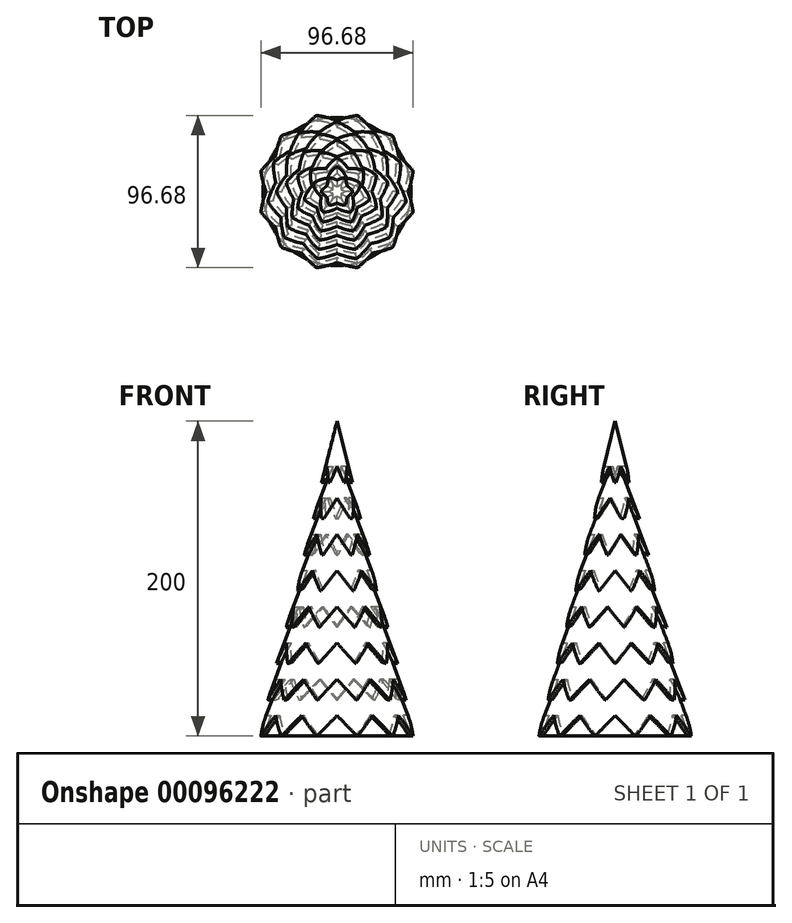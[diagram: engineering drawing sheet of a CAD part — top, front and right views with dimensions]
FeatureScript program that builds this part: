
annotation { "Feature Type Name" : "Feature", "Feature Type Description" : "" }
export const myFeature = defineFeature(function(context is Context, id is Id, definition is map)
    precondition{}
    {
        {
            var Q0;
            Q0=qCreatedBy(makeId("Front.planeOp"),FACE);
            var sketch = newSketch(context, id + "F0", { "sketchPlane" : qUnion([Q0])});
            skLineSegment(sketch, "E0", {"start": v(0, 0) * mm, "end": v(0, 200) * mm});
            skLineSegment(sketch, "E1", {"start": v(-50, 0) * mm, "end": v(0, 0) * mm});
            skLineSegment(sketch, "E2", {"start": v(-50, 0) * mm, "end": v(-41.24, 23.03) * mm});
            skLineSegment(sketch, "E3", {"start": v(-41.24, 23.03) * mm, "end": v(-44.24, 23.03) * mm});
            skLineSegment(sketch, "E4", {"start": v(-44.24, 23.03) * mm, "end": v(-35.49, 46.06) * mm});
            skLineSegment(sketch, "E5", {"start": v(-35.49, 46.06) * mm, "end": v(-38.49, 46.06) * mm});
            skLineSegment(sketch, "E6", {"start": v(-38.49, 46.06) * mm, "end": v(-29.73, 69.08) * mm});
            skLineSegment(sketch, "E7", {"start": v(-29.73, 69.08) * mm, "end": v(-32.73, 69.08) * mm});
            skLineSegment(sketch, "E8", {"start": v(-32.73, 69.08) * mm, "end": v(-23.97, 92.11) * mm});
            skLineSegment(sketch, "E9", {"start": v(-23.97, 92.11) * mm, "end": v(-26.97, 92.11) * mm});
            skLineSegment(sketch, "E10", {"start": v(-26.97, 92.11) * mm, "end": v(-18.22, 115.14) * mm});
            skLineSegment(sketch, "E11", {"start": v(-18.22, 115.14) * mm, "end": v(-21.22, 115.14) * mm});
            skLineSegment(sketch, "E12", {"start": v(-21.22, 115.14) * mm, "end": v(-12.46, 138.17) * mm});
            skLineSegment(sketch, "E13", {"start": v(-12.46, 138.17) * mm, "end": v(-15.46, 138.17) * mm});
            skLineSegment(sketch, "E14", {"start": v(-15.46, 138.17) * mm, "end": v(-6.7, 161.2) * mm});
            skLineSegment(sketch, "E15", {"start": v(-6.7, 161.2) * mm, "end": v(-9.7, 161.2) * mm});
            skLineSegment(sketch, "E16", {"start": v(-9.7, 161.2) * mm, "end": v(0, 200) * mm});
            skLineSegment(sketch, "E17", {"start": v(-50, 0) * mm, "end": v(0, 200) * mm, "construction": true});
            skLineSegment(sketch, "E18.0", {"start": v(-53.2, 0) * mm, "end": v(-48.27, 13) * mm});
            skLineSegment(sketch, "E19", {"start": v(-53.2, 0) * mm, "end": v(-50, 0) * mm});
            skLineSegment(sketch, "E20", {"start": v(-48.27, 13) * mm, "end": v(-45.06, 13) * mm});
            skSolve(sketch);
        }
        {
            var Q0;
            Q0=makeQuery(id+"F0.imprint","IMPRINT",FACE,{"disambiguationData":[TD([[makeQuery(id+"F0.imprint","IMPRINT",EDGE,{"derivedFrom":sQuery(id+"F0.wireOp",EDGE,"E0")}),1.0]])]});
            var Q1;
            Q1=sQuery(id+"F0.wireOp",EDGE,"E0");
            revolve(context, id + "F1", {"entities" : qUnion([Q0]), "axis" : qUnion([Q1]), "revolveType" : RevolveType.FULL});
        }
        {
            var Q0;
            Q0=qCreatedBy(makeId("Front.planeOp"),FACE);
            var sketch = newSketch(context, id + "F2", { "sketchPlane" : qUnion([Q0])});
            skLineSegment(sketch, "E21", {"start": v(-12.78, 0) * mm, "end": v(12.78, 0) * mm});
            skLineSegment(sketch, "E22", {"start": v(12.78, 0) * mm, "end": v(0, 13) * mm});
            skLineSegment(sketch, "E23", {"start": v(0, 13) * mm, "end": v(-12.78, 0) * mm});
            skLineSegment(sketch, "E24.direction1", {"start": v(-12.78, 0) * mm, "end": v(12.78, 0) * mm, "construction": true});
            skLineSegment(sketch, "E24.direction2", {"start": v(-12.78, 0) * mm, "end": v(-12.78, 23.03) * mm, "construction": true});
            skLineSegment(sketch, "E25", {"start": v(-8.28, 138.17) * mm, "end": v(8.28, 138.17) * mm});
            skLineSegment(sketch, "E26", {"start": v(8.28, 138.17) * mm, "end": v(0, 151.17) * mm});
            skLineSegment(sketch, "E27", {"start": v(0, 151.17) * mm, "end": v(-8.28, 138.17) * mm});
            skLineSegment(sketch, "E28", {"start": v(-4.35, 161.2) * mm, "end": v(4.35, 161.2) * mm});
            skLineSegment(sketch, "E29", {"start": v(4.35, 161.2) * mm, "end": v(0, 171.2) * mm});
            skLineSegment(sketch, "E30", {"start": v(0, 171.2) * mm, "end": v(-4.35, 161.2) * mm});
            skLineSegment(sketch, "E31", {"start": v(-12.12, 23.03) * mm, "end": v(12.12, 23.03) * mm});
            skLineSegment(sketch, "E32", {"start": v(12.12, 23.03) * mm, "end": v(0, 36.03) * mm});
            skLineSegment(sketch, "E33", {"start": v(0, 36.03) * mm, "end": v(-12.12, 23.03) * mm});
            skLineSegment(sketch, "E34", {"start": v(-11.7, 46.06) * mm, "end": v(11.7, 46.06) * mm});
            skLineSegment(sketch, "E35", {"start": v(11.7, 46.06) * mm, "end": v(0, 59.06) * mm});
            skLineSegment(sketch, "E36", {"start": v(0, 59.06) * mm, "end": v(-11.7, 46.06) * mm});
            skLineSegment(sketch, "E37", {"start": v(-11.1, 69.08) * mm, "end": v(11.1, 69.08) * mm});
            skLineSegment(sketch, "E38", {"start": v(11.1, 69.08) * mm, "end": v(0, 82.08) * mm});
            skLineSegment(sketch, "E39", {"start": v(0, 82.08) * mm, "end": v(-11.1, 69.08) * mm});
            skLineSegment(sketch, "E40", {"start": v(-10.16, 92.11) * mm, "end": v(10.16, 92.11) * mm});
            skLineSegment(sketch, "E41", {"start": v(10.16, 92.11) * mm, "end": v(0, 105.11) * mm});
            skLineSegment(sketch, "E42", {"start": v(0, 105.11) * mm, "end": v(-10.16, 92.11) * mm});
            skLineSegment(sketch, "E43", {"start": v(-8.77, 115.14) * mm, "end": v(8.77, 115.14) * mm});
            skLineSegment(sketch, "E44", {"start": v(-8.77, 115.14) * mm, "end": v(0, 128.14) * mm});
            skLineSegment(sketch, "E45", {"start": v(0, 128.14) * mm, "end": v(8.77, 115.14) * mm});
            skSolve(sketch);
        }
        {
            var Q0;
            Q0=makeQuery(id+"F2.imprint","IMPRINT",FACE,{"disambiguationData":[TD([[makeQuery(id+"F2.imprint","IMPRINT",EDGE,{"derivedFrom":sQuery(id+"F2.wireOp",EDGE,"E21")}),1.0]])]});
            var Q1;
            Q1=makeQuery(id+"F1.opRevolve","SWEPT_FACE",FACE,{"disambiguationData":[OSD([sQuery(id+"F0.wireOp",EDGE,"E4")])]});
            var Q2;
            Q2=makeQuery(id+"F1.opRevolve","SWEPT_FACE",FACE,{"disambiguationData":[OSD([sQuery(id+"F0.wireOp",EDGE,"E2")])]});
            extrude(context, id + "F3", {"entities" : qUnion([Q0]), "endBound" : BoundingType.UP_TO_SURFACE, "endBoundEntityFace" : qUnion([Q1]), "depth" : 25 * mm, "hasSecondDirection" : true, "secondDirectionBound" : SecondDirectionBoundingType.UP_TO_SURFACE, "secondDirectionOppositeDirection" : false, "secondDirectionBoundEntityFace" : qUnion([Q2]), "secondDirectionDepth" : 25 * mm});
        }
        {
            var Q0;
            Q0=makeQuery(id+"F2.imprint","IMPRINT",FACE,{"disambiguationData":[TD([[makeQuery(id+"F2.imprint","IMPRINT",EDGE,{"derivedFrom":sQuery(id+"F2.wireOp",EDGE,"E31")}),1.0]])]});
            var Q1;
            Q1=makeQuery(id+"F1.opRevolve","SWEPT_FACE",FACE,{"disambiguationData":[OSD([sQuery(id+"F0.wireOp",EDGE,"E4")])]});
            var Q2;
            Q2=makeQuery(id+"F1.opRevolve","SWEPT_FACE",FACE,{"disambiguationData":[OSD([sQuery(id+"F0.wireOp",EDGE,"E2")])]});
            extrude(context, id + "F4", {"entities" : qUnion([Q0]), "endBound" : BoundingType.UP_TO_SURFACE, "endBoundEntityFace" : qUnion([Q1]), "depth" : 25 * mm, "hasSecondDirection" : true, "secondDirectionBound" : SecondDirectionBoundingType.UP_TO_SURFACE, "secondDirectionOppositeDirection" : false, "secondDirectionBoundEntityFace" : qUnion([Q2]), "secondDirectionDepth" : 25 * mm});
        }
        {
            var Q0;
            Q0=makeQuery(id+"F2.imprint","IMPRINT",FACE,{"disambiguationData":[TD([[makeQuery(id+"F2.imprint","IMPRINT",EDGE,{"derivedFrom":sQuery(id+"F2.wireOp",EDGE,"E34")}),1.0]])]});
            var Q1;
            Q1=makeQuery(id+"F1.opRevolve","SWEPT_FACE",FACE,{"disambiguationData":[OSD([sQuery(id+"F0.wireOp",EDGE,"E6")])]});
            var Q2;
            Q2=makeQuery(id+"F1.opRevolve","SWEPT_FACE",FACE,{"disambiguationData":[OSD([sQuery(id+"F0.wireOp",EDGE,"E4")])]});
            extrude(context, id + "F5", {"entities" : qUnion([Q0]), "endBound" : BoundingType.UP_TO_SURFACE, "endBoundEntityFace" : qUnion([Q1]), "depth" : 25 * mm, "hasSecondDirection" : true, "secondDirectionBound" : SecondDirectionBoundingType.UP_TO_SURFACE, "secondDirectionOppositeDirection" : false, "secondDirectionBoundEntityFace" : qUnion([Q2]), "secondDirectionDepth" : 25 * mm});
        }
        {
            var Q0;
            Q0=makeQuery(id+"F2.imprint","IMPRINT",FACE,{"disambiguationData":[TD([[makeQuery(id+"F2.imprint","IMPRINT",EDGE,{"derivedFrom":sQuery(id+"F2.wireOp",EDGE,"E37")}),1.0]])]});
            var Q1;
            Q1=makeQuery(id+"F1.opRevolve","SWEPT_FACE",FACE,{"disambiguationData":[OSD([sQuery(id+"F0.wireOp",EDGE,"E8")])]});
            var Q2;
            Q2=makeQuery(id+"F1.opRevolve","SWEPT_FACE",FACE,{"disambiguationData":[OSD([sQuery(id+"F0.wireOp",EDGE,"E6")])]});
            extrude(context, id + "F6", {"entities" : qUnion([Q0]), "endBound" : BoundingType.UP_TO_SURFACE, "endBoundEntityFace" : qUnion([Q1]), "depth" : 25 * mm, "hasSecondDirection" : true, "secondDirectionBound" : SecondDirectionBoundingType.UP_TO_SURFACE, "secondDirectionOppositeDirection" : false, "secondDirectionBoundEntityFace" : qUnion([Q2]), "secondDirectionDepth" : 25 * mm});
        }
        {
            var Q0;
            Q0=makeQuery(id+"F2.imprint","IMPRINT",FACE,{"disambiguationData":[TD([[makeQuery(id+"F2.imprint","IMPRINT",EDGE,{"derivedFrom":sQuery(id+"F2.wireOp",EDGE,"E40")}),1.0]])]});
            var Q1;
            Q1=makeQuery(id+"F1.opRevolve","SWEPT_FACE",FACE,{"disambiguationData":[OSD([sQuery(id+"F0.wireOp",EDGE,"E10")])]});
            var Q2;
            Q2=makeQuery(id+"F1.opRevolve","SWEPT_FACE",FACE,{"disambiguationData":[OSD([sQuery(id+"F0.wireOp",EDGE,"E8")])]});
            extrude(context, id + "F7", {"entities" : qUnion([Q0]), "endBound" : BoundingType.UP_TO_SURFACE, "endBoundEntityFace" : qUnion([Q1]), "depth" : 25 * mm, "hasSecondDirection" : true, "secondDirectionBound" : SecondDirectionBoundingType.UP_TO_SURFACE, "secondDirectionOppositeDirection" : false, "secondDirectionBoundEntityFace" : qUnion([Q2]), "secondDirectionDepth" : 25 * mm});
        }
        {
            var Q0;
            Q0=makeQuery(id+"F2.imprint","IMPRINT",FACE,{"disambiguationData":[TD([[makeQuery(id+"F2.imprint","IMPRINT",EDGE,{"derivedFrom":sQuery(id+"F2.wireOp",EDGE,"E43")}),1.0]])]});
            var Q1;
            Q1=makeQuery(id+"F1.opRevolve","SWEPT_FACE",FACE,{"disambiguationData":[OSD([sQuery(id+"F0.wireOp",EDGE,"E12")])]});
            var Q2;
            Q2=makeQuery(id+"F1.opRevolve","SWEPT_FACE",FACE,{"disambiguationData":[OSD([sQuery(id+"F0.wireOp",EDGE,"E10")])]});
            extrude(context, id + "F8", {"entities" : qUnion([Q0]), "endBound" : BoundingType.UP_TO_SURFACE, "endBoundEntityFace" : qUnion([Q1]), "depth" : 25 * mm, "hasSecondDirection" : true, "secondDirectionBound" : SecondDirectionBoundingType.UP_TO_SURFACE, "secondDirectionOppositeDirection" : false, "secondDirectionBoundEntityFace" : qUnion([Q2]), "secondDirectionDepth" : 25 * mm});
        }
        {
            var Q0;
            Q0=makeQuery(id+"F2.imprint","IMPRINT",FACE,{"disambiguationData":[TD([[makeQuery(id+"F2.imprint","IMPRINT",EDGE,{"derivedFrom":sQuery(id+"F2.wireOp",EDGE,"E25")}),1.0]])]});
            var Q1;
            Q1=makeQuery(id+"F1.opRevolve","SWEPT_FACE",FACE,{"disambiguationData":[OSD([sQuery(id+"F0.wireOp",EDGE,"E14")])]});
            var Q2;
            Q2=makeQuery(id+"F1.opRevolve","SWEPT_FACE",FACE,{"disambiguationData":[OSD([sQuery(id+"F0.wireOp",EDGE,"E12")])]});
            extrude(context, id + "F9", {"entities" : qUnion([Q0]), "endBound" : BoundingType.UP_TO_SURFACE, "endBoundEntityFace" : qUnion([Q1]), "depth" : 25 * mm, "hasSecondDirection" : true, "secondDirectionBound" : SecondDirectionBoundingType.UP_TO_SURFACE, "secondDirectionOppositeDirection" : false, "secondDirectionBoundEntityFace" : qUnion([Q2]), "secondDirectionDepth" : 25 * mm});
        }
        {
            var Q0;
            Q0=makeQuery(id+"F2.imprint","IMPRINT",FACE,{"disambiguationData":[TD([[makeQuery(id+"F2.imprint","IMPRINT",EDGE,{"derivedFrom":sQuery(id+"F2.wireOp",EDGE,"E28")}),1.0]])]});
            var Q1;
            Q1=makeQuery(id+"F1.opRevolve","SWEPT_FACE",FACE,{"disambiguationData":[OSD([sQuery(id+"F0.wireOp",EDGE,"E16")])]});
            var Q2;
            Q2=makeQuery(id+"F1.opRevolve","SWEPT_FACE",FACE,{"disambiguationData":[OSD([sQuery(id+"F0.wireOp",EDGE,"E14")])]});
            extrude(context, id + "F10", {"entities" : qUnion([Q0]), "endBound" : BoundingType.UP_TO_SURFACE, "endBoundEntityFace" : qUnion([Q1]), "depth" : 25 * mm, "hasSecondDirection" : true, "secondDirectionBound" : SecondDirectionBoundingType.UP_TO_SURFACE, "secondDirectionOppositeDirection" : false, "secondDirectionBoundEntityFace" : qUnion([Q2]), "secondDirectionDepth" : 25 * mm});
        }
        {
            var Q0;
            Q0=makeQuery(id+"F4.opExtrude","SWEPT_BODY",BODY,{"disambiguationData":[OSD([sQuery(id+"F2.wireOp",EDGE,"E31"),sQuery(id+"F2.wireOp",EDGE,"E32"),sQuery(id+"F2.wireOp",EDGE,"E33")])]});
            var Q1;
            Q1=makeQuery(id+"F1.opRevolve","SWEPT_EDGE",EDGE,{"disambiguationData":[OSD([sQuery(id+"F0.wireOp",EDGE,"E3"),sQuery(id+"F0.wireOp",EDGE,"E4")])]});
            circularPattern(context, id + "F11", {"operationType" : NewBodyOperationType.REMOVE, "entities" : qUnion([Q0]), "axis" : qUnion([Q1]), "angle" : 360 * degree, "instanceCount" : 11, "equalSpace" : true});
        }
        {
            var Q0;
            Q0=makeQuery(id+"F5.opExtrude","SWEPT_BODY",BODY,{"disambiguationData":[OSD([sQuery(id+"F2.wireOp",EDGE,"E34"),sQuery(id+"F2.wireOp",EDGE,"E35"),sQuery(id+"F2.wireOp",EDGE,"E36")])]});
            var Q1;
            Q1=makeQuery(id+"F1.opRevolve","SWEPT_EDGE",EDGE,{"disambiguationData":[OSD([sQuery(id+"F0.wireOp",EDGE,"E5"),sQuery(id+"F0.wireOp",EDGE,"E6")])]});
            circularPattern(context, id + "F12", {"operationType" : NewBodyOperationType.REMOVE, "entities" : qUnion([Q0]), "axis" : qUnion([Q1]), "angle" : 360 * degree, "instanceCount" : 10, "equalSpace" : true});
        }
        {
            var Q0;
            Q0=makeQuery(id+"F6.opExtrude","SWEPT_BODY",BODY,{"disambiguationData":[OSD([sQuery(id+"F2.wireOp",EDGE,"E37"),sQuery(id+"F2.wireOp",EDGE,"E38"),sQuery(id+"F2.wireOp",EDGE,"E39")])]});
            var Q1;
            Q1=makeQuery(id+"F1.opRevolve","SWEPT_EDGE",EDGE,{"disambiguationData":[OSD([sQuery(id+"F0.wireOp",EDGE,"E7"),sQuery(id+"F0.wireOp",EDGE,"E8")])]});
            circularPattern(context, id + "F13", {"operationType" : NewBodyOperationType.REMOVE, "entities" : qUnion([Q0]), "axis" : qUnion([Q1]), "angle" : 360 * degree, "instanceCount" : 9, "equalSpace" : true});
        }
        {
            var Q0;
            Q0=makeQuery(id+"F7.opExtrude","SWEPT_BODY",BODY,{"disambiguationData":[OSD([sQuery(id+"F2.wireOp",EDGE,"E40"),sQuery(id+"F2.wireOp",EDGE,"E41"),sQuery(id+"F2.wireOp",EDGE,"E42")])]});
            var Q1;
            Q1=makeQuery(id+"F1.opRevolve","SWEPT_EDGE",EDGE,{"disambiguationData":[OSD([sQuery(id+"F0.wireOp",EDGE,"E9"),sQuery(id+"F0.wireOp",EDGE,"E10")])]});
            circularPattern(context, id + "F14", {"operationType" : NewBodyOperationType.REMOVE, "entities" : qUnion([Q0]), "axis" : qUnion([Q1]), "angle" : 360 * degree, "instanceCount" : 8, "equalSpace" : true});
        }
        {
            var Q0;
            Q0=makeQuery(id+"F8.opExtrude","SWEPT_BODY",BODY,{"disambiguationData":[OSD([sQuery(id+"F2.wireOp",EDGE,"E43"),sQuery(id+"F2.wireOp",EDGE,"E44"),sQuery(id+"F2.wireOp",EDGE,"E45")])]});
            var Q1;
            Q1=makeQuery(id+"F1.opRevolve","SWEPT_EDGE",EDGE,{"disambiguationData":[OSD([sQuery(id+"F0.wireOp",EDGE,"E11"),sQuery(id+"F0.wireOp",EDGE,"E12")])]});
            circularPattern(context, id + "F15", {"operationType" : NewBodyOperationType.REMOVE, "entities" : qUnion([Q0]), "axis" : qUnion([Q1]), "angle" : 360 * degree, "instanceCount" : 7, "equalSpace" : true});
        }
        {
            var Q0;
            Q0=makeQuery(id+"F9.opExtrude","SWEPT_BODY",BODY,{"disambiguationData":[OSD([sQuery(id+"F2.wireOp",EDGE,"E25"),sQuery(id+"F2.wireOp",EDGE,"E26"),sQuery(id+"F2.wireOp",EDGE,"E27")])]});
            var Q1;
            Q1=makeQuery(id+"F1.opRevolve","SWEPT_EDGE",EDGE,{"disambiguationData":[OSD([sQuery(id+"F0.wireOp",EDGE,"E13"),sQuery(id+"F0.wireOp",EDGE,"E14")])]});
            circularPattern(context, id + "F16", {"operationType" : NewBodyOperationType.REMOVE, "entities" : qUnion([Q0]), "axis" : qUnion([Q1]), "angle" : 360 * degree, "instanceCount" : 5, "equalSpace" : true});
        }
        {
            var Q0;
            Q0=makeQuery(id+"F10.opExtrude","SWEPT_BODY",BODY,{"disambiguationData":[OSD([sQuery(id+"F2.wireOp",EDGE,"E28"),sQuery(id+"F2.wireOp",EDGE,"E29"),sQuery(id+"F2.wireOp",EDGE,"E30")])]});
            var Q1;
            Q1=makeQuery(id+"F1.opRevolve","SWEPT_EDGE",EDGE,{"disambiguationData":[OSD([sQuery(id+"F0.wireOp",EDGE,"E15"),sQuery(id+"F0.wireOp",EDGE,"E16")])]});
            circularPattern(context, id + "F17", {"operationType" : NewBodyOperationType.REMOVE, "entities" : qUnion([Q0]), "axis" : qUnion([Q1]), "angle" : 360 * degree, "instanceCount" : 6, "equalSpace" : true});
        }
        {
            var Q0;
            Q0=makeQuery(id+"F3.opExtrude","SWEPT_BODY",BODY,{"disambiguationData":[OSD([sQuery(id+"F2.wireOp",EDGE,"E21"),sQuery(id+"F2.wireOp",EDGE,"E22"),sQuery(id+"F2.wireOp",EDGE,"E23")])]});
            transform(context, id + "F18", {"entities" : qUnion([Q0]), "transformType" : TransformType.TRANSLATION_3D, "dx" : 0 * mm, "dy" : 3 * mm, "dz" : 0 * mm, "makeCopy" : false});
        }
        {
            var Q0;
            Q0=makeQuery(id+"F3.opExtrude","SWEPT_BODY",BODY,{"disambiguationData":[OSD([sQuery(id+"F2.wireOp",EDGE,"E21"),sQuery(id+"F2.wireOp",EDGE,"E22"),sQuery(id+"F2.wireOp",EDGE,"E23")])]});
            var Q1;
            Q1=makeQuery(id+"F1.opRevolve","SWEPT_EDGE",EDGE,{"disambiguationData":[OSD([sQuery(id+"F0.wireOp",EDGE,"E1"),sQuery(id+"F0.wireOp",EDGE,"E2"),sQuery(id+"F0.wireOp",EDGE,"E19")])]});
            circularPattern(context, id + "F19", {"operationType" : NewBodyOperationType.REMOVE, "entities" : qUnion([Q0]), "axis" : qUnion([Q1]), "angle" : 360 * degree, "instanceCount" : 12, "equalSpace" : true});
        }
    });
